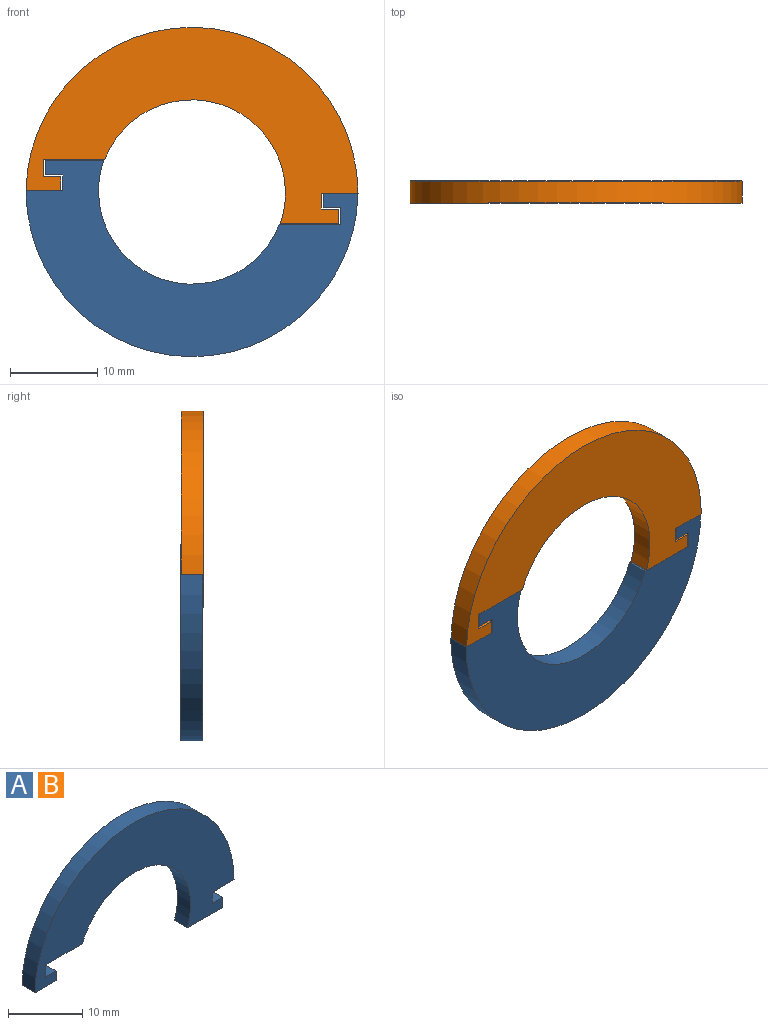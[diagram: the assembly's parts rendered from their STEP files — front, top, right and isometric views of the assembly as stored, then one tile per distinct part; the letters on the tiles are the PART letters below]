
ASSEMBLY  parts=2 mates=1
PART A: 14 faces, bbox 38x2.5x22.5 mm
  f0: cylinder r=10.7mm len=20.66mm, axis (0,1,0), area 83mm2, adj f1,f11,f12,f13
  f1: plane 6.69x2.5mm, normal (0,0,-1), area 16.7mm2, adj f0,f2,f12,f13
  f2: plane 2.5x1.7mm, normal (1,0,0), area 4.3mm2, adj f1,f3,f12,f13
  f3: plane 2.5x2mm, normal (0,0,1), area 5mm2, adj f2,f4,f12,f13
  f4: plane 2.5x1.8mm, normal (1,0,0), area 4.5mm2, adj f3,f5,f12,f13
  f5: plane 4.2x2.5mm, normal (0,0,-1), area 10.5mm2, adj f4,f6,f12,f13
  f6: cylinder r=19mm len=38mm, axis (0,1,0), area 148.5mm2, adj f5,f7,f12,f13
  f7: plane 4x2.5mm, normal (0,0,-1), area 10mm2, adj f6,f8,f12,f13
  f8: plane 2.5x1.6mm, normal (1,0,0), area 4mm2, adj f7,f9,f12,f13
  f9: plane 2.5x2mm, normal (0,0,1), area 5mm2, adj f8,f10,f12,f13
  f10: plane 2.5x2mm, normal (1,0,0), area 5mm2, adj f9,f11,f12,f13
  f11: plane 7.03x2.5mm, normal (0,0,-1), area 17.6mm2, adj f0,f10,f12,f13
  f12: plane 38x22.5mm, normal (0,-1,0), area 382.7mm2, adj f0,f1,f2,f3,f4,f5,f6,f7
  f13: plane 38x22.5mm, normal (0,1,0), area 382.7mm2, adj f0,f1,f2,f3,f4,f5,f6,f7
PART B: same geometry as A
PLACE A rot(axis=(0,1,0),180deg) t=(0.51,2.13,-0.47)mm
PLACE B t=(0.51,2.06,-0.77)mm
MATE slider A.f12 <-> B.f12  axis (0,-1,0) through (19.51,0.88,-0.77)mm
